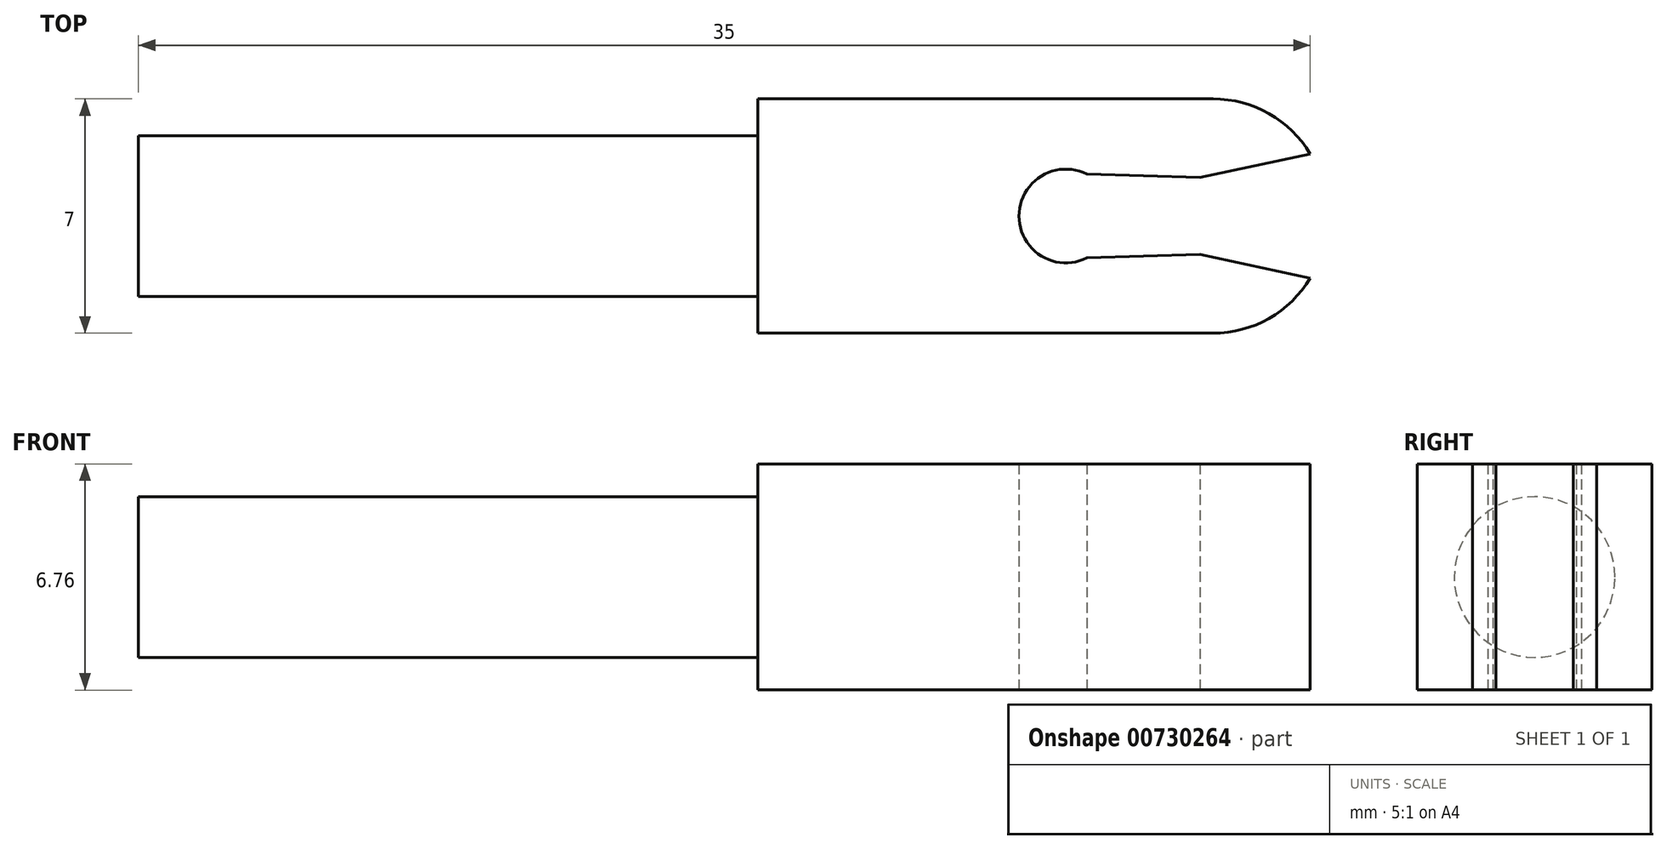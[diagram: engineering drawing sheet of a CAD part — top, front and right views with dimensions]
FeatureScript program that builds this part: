
annotation { "Feature Type Name" : "Feature", "Feature Type Description" : "" }
export const myFeature = defineFeature(function(context is Context, id is Id, definition is map)
    precondition{}
    {
        {
            var Q0;
            Q0=qCreatedBy(makeId("Top.planeOp"),FACE);
            var sketch = newSketch(context, id + "F0", { "sketchPlane" : qUnion([Q0])});
            skLineSegment(sketch, "E0.bottom", {"start": v(0, 3.5) * mm, "end": v(16.5, 3.5) * mm});
            skLineSegment(sketch, "E0.top", {"start": v(0, -3.5) * mm, "end": v(16.5, -3.5) * mm});
            skLineSegment(sketch, "E0.left", {"start": v(0, 3.5) * mm, "end": v(0, -3.5) * mm});
            skLineSegment(sketch, "E0.right", {"start": v(16.5, 3.5) * mm, "end": v(16.5, -3.5) * mm});
            skLineSegment(sketch, "E1.bottom", {"start": v(0, 2.35) * mm, "end": v(-18.5, 2.35) * mm});
            skLineSegment(sketch, "E1.top", {"start": v(0, -2.35) * mm, "end": v(-18.5, -2.35) * mm});
            skLineSegment(sketch, "E1.left", {"start": v(0, 2.35) * mm, "end": v(0, -2.35) * mm});
            skLineSegment(sketch, "E1.right", {"start": v(-18.5, 2.35) * mm, "end": v(-18.5, -2.35) * mm});
            skCircle(sketch, "E2", {"center": v(9.2, 0) * mm, "radius": 1.4 * mm});
            skPoint(sketch, "E3", {"position": v(13.2, 0) * mm});
            skPoint(sketch, "E4", {"position": v(7.8, 0) * mm});
            skPoint(sketch, "E5", {"position": v(16.5, 1.85) * mm});
            skPoint(sketch, "E6.MirrorP", {"position": v(16.5, -1.85) * mm});
            skPoint(sketch, "E7", {"position": v(13.2, 1.15) * mm});
            skPoint(sketch, "E8.MirrorP", {"position": v(13.2, -1.15) * mm});
            skLineSegment(sketch, "E9", {"start": v(16.5, 1.85) * mm, "end": v(13.2, 1.15) * mm});
            skLineSegment(sketch, "E10", {"start": v(13.2, -1.15) * mm, "end": v(16.5, -1.85) * mm});
            skPoint(sketch, "E11", {"position": v(9.83, 1.25) * mm});
            skPoint(sketch, "E12.MirrorP", {"position": v(9.83, -1.25) * mm});
            skLineSegment(sketch, "E13", {"start": v(9.83, 1.25) * mm, "end": v(13.2, 1.15) * mm});
            skLineSegment(sketch, "E14", {"start": v(9.83, -1.25) * mm, "end": v(13.2, -1.15) * mm});
            skSolve(sketch);
        }
        {
            var Q0;
            {var subQ4=sQuery(id+"F0.wireOp",EDGE,"E0.bottom");Q0=makeQuery(id+"F0.imprint","IMPRINT",FACE,{"disambiguationData":[TD([[makeQuery(id+"F0.imprint","IMPRINT",EDGE,{"derivedFrom":subQ4}),-1.0]])]});}
            extrude(context, id + "F1", {"entities" : qUnion([Q0]), "depth" : 3.38 * mm, "offsetDistance" : 25 * mm, "hasSecondDirection" : true, "secondDirectionOppositeDirection" : true, "secondDirectionDepth" : 3.38 * mm});
        }
        {
            var Q0;
            Q0=makeQuery(id+"F1.opExtrude","SWEPT_FACE",FACE,{"disambiguationData":[OSD([sQuery(id+"F0.wireOp",EDGE,"E0.left"),sQuery(id+"F0.wireOp",EDGE,"E1.left")])]});
            var sketch = newSketch(context, id + "F2", { "sketchPlane" : qUnion([Q0])});
            skCircle(sketch, "E15", {"center": v(0, 0) * mm, "radius": 2.4 * mm});
            skSolve(sketch);
        }
        {
            var Q0;
            Q0=makeQuery(id+"F2.imprint","IMPRINT",FACE,{"disambiguationData":[TD([[makeQuery(id+"F2.imprint","IMPRINT",EDGE,{"derivedFrom":sQuery(id+"F2.wireOp",EDGE,"E15")}),1.0]])]});
            extrude(context, id + "F3", {"entities" : qUnion([Q0]), "operationType" : NewBodyOperationType.ADD, "depth" : 18.5 * mm, "offsetDistance" : 25 * mm});
        }
        {
            var Q0;
            Q0=makeQuery(id+"F1.opExtrude","SWEPT_EDGE",EDGE,{"disambiguationData":[OSD([sQuery(id+"F0.wireOp",EDGE,"E0.top"),sQuery(id+"F0.wireOp",EDGE,"E0.right")])]});
            var Q1;
            Q1=makeQuery(id+"F1.opExtrude","SWEPT_EDGE",EDGE,{"disambiguationData":[OSD([sQuery(id+"F0.wireOp",EDGE,"E0.bottom"),sQuery(id+"F0.wireOp",EDGE,"E0.right")])]});
            fillet(context, id + "F4", {"entities" : qUnion([Q0, Q1]), "radius" : 3.38 * mm, "tangentPropagation" : true, "allowEdgeOverflow" : false});
        }
    });
